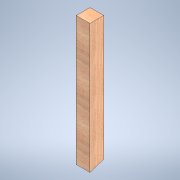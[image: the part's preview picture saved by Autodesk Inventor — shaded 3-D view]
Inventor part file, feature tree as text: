
AUTODESK INVENTOR PART (.ipt)
format: ipt  version: 2020.2 (Build 242310000, 310)  size: 120,320 bytes
history: native  units: in
note: dims shown in document units (in); Inventor stores cm internally (conversion verified against a paired STEP export)
features: extrude x1, sketch x1
ambient origin geometry x8: Origin, YZ Plane, XZ Plane, XY Plane, X Axis, Y Axis, Z Axis, Center Point
bodies: Solid1 (feature_tree)
feature tree (2):
  extrude  "Extrusion1"  TaperAngle=0.0deg  [1 undecoded]
  sketch  "Sketch1"  dims[d3=3.5in d4=0.0in]
note: 1 required parameter value undecoded (feature->parameter linkage not recoverable at this tier; creation-order binding heuristic only, values carry confidence <= 0.55)
